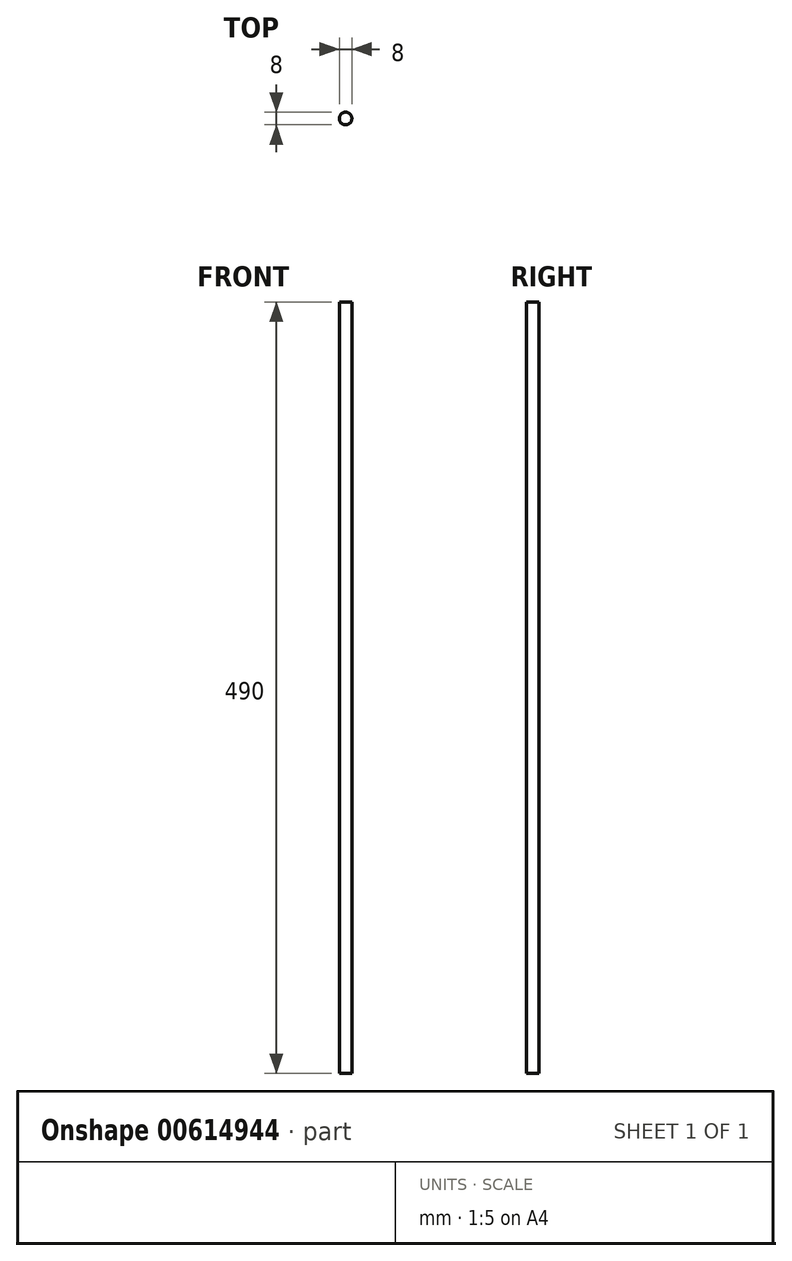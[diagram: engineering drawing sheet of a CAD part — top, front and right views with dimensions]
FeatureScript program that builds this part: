
annotation { "Feature Type Name" : "Feature", "Feature Type Description" : "" }
export const myFeature = defineFeature(function(context is Context, id is Id, definition is map)
    precondition{}
    {
        {
            var Q0;
            Q0=qCreatedBy(makeId("Top.planeOp"),FACE);
            var sketch = newSketch(context, id + "F0", { "sketchPlane" : qUnion([Q0])});
            skCircle(sketch, "E0", {"center": v(0, 0) * mm, "radius": 4 * mm});
            skSolve(sketch);
        }
        {
            var Q0;
            Q0 = qSketchRegion(id + "F0", true);
            extrude(context, id + "F1", {"entities" : qUnion([Q0]), "depth" : 490 * mm, "offsetDistance" : 25 * mm});
        }
    });
